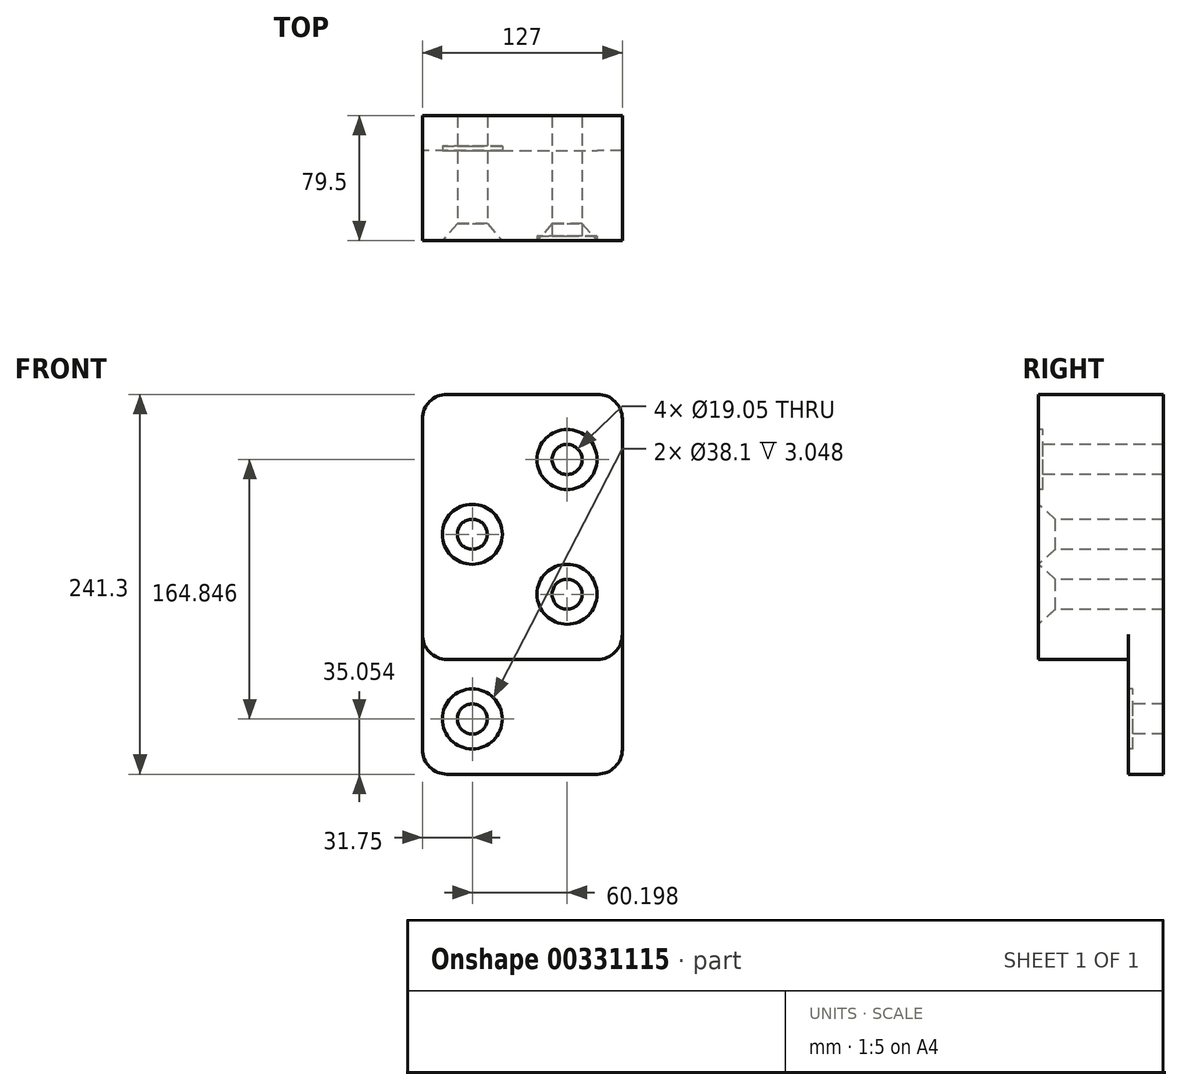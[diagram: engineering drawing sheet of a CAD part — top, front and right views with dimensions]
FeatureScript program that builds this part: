
annotation { "Feature Type Name" : "Feature", "Feature Type Description" : "" }
export const myFeature = defineFeature(function(context is Context, id is Id, definition is map)
    precondition{}
    {
        {
            var Q0;
            Q0=qCreatedBy(makeId("Front.planeOp"),FACE);
            var sketch = newSketch(context, id + "F0", { "sketchPlane" : qUnion([Q0])});
            skLineSegment(sketch, "E0.bottom", {"start": v(0, 0) * mm, "end": v(127, 0) * mm});
            skLineSegment(sketch, "E0.top", {"start": v(0, 168.4) * mm, "end": v(127, 168.4) * mm});
            skLineSegment(sketch, "E0.left", {"start": v(0, 0) * mm, "end": v(0, 168.4) * mm});
            skLineSegment(sketch, "E0.right", {"start": v(127, 0) * mm, "end": v(127, 168.4) * mm});
            skCircle(sketch, "E1", {"center": v(91.95, 41.4) * mm, "radius": 9.53 * mm});
            skCircle(sketch, "E2", {"center": v(91.95, 127) * mm, "radius": 9.53 * mm});
            skCircle(sketch, "E3", {"center": v(31.75, 79.5) * mm, "radius": 9.53 * mm});
            skSolve(sketch);
        }
        {
            var Q0;
            Q0=makeQuery(id+"F0.imprint","IMPRINT",FACE,{"disambiguationData":[TD([[makeQuery(id+"F0.imprint","IMPRINT",EDGE,{"derivedFrom":sQuery(id+"F0.wireOp",EDGE,"E0.top")}),-1.0]])]});
            var Q1;
            Q1=makeQuery(id+"F0.imprint","IMPRINT",FACE,{"disambiguationData":[TD([[makeQuery(id+"F0.imprint","IMPRINT",EDGE,{"derivedFrom":sQuery(id+"F0.wireOp",EDGE,"E2")}),1.0]])]});
            var Q2;
            Q2=makeQuery(id+"F0.imprint","IMPRINT",FACE,{"disambiguationData":[TD([[makeQuery(id+"F0.imprint","IMPRINT",EDGE,{"derivedFrom":sQuery(id+"F0.wireOp",EDGE,"E3")}),1.0]])]});
            var Q3;
            Q3=makeQuery(id+"F0.imprint","IMPRINT",FACE,{"disambiguationData":[TD([[makeQuery(id+"F0.imprint","IMPRINT",EDGE,{"derivedFrom":sQuery(id+"F0.wireOp",EDGE,"E1")}),1.0]])]});
            extrude(context, id + "F1", {"entities" : qUnion([Q0, Q1, Q2, Q3]), "oppositeDirection" : true, "depth" : 79.5 * mm});
        }
        {
            var Q0;
            Q0=sQuery(id+"F0.wireOp",VERTEX,"E3.center");
            var Q1;
            Q1=sQuery(id+"F0.wireOp",VERTEX,"E1.center");
            var Q2;
            Q2=makeQuery(id+"F1.opExtrude","SWEPT_BODY",BODY,{"disambiguationData":[OSD([sQuery(id+"F0.wireOp",EDGE,"E0.top"),sQuery(id+"F0.wireOp",EDGE,"E0.left"),sQuery(id+"F0.wireOp",EDGE,"E0.right"),sQuery(id+"F0.wireOp",EDGE,"PMlJOAfA-4wVx-9Cpc-nXHO-quy2oaBIfGFF.bottom")])]});
            hole(context, id + "F2", {"style" : HoleStyle.C_SINK, "endStyle" : HoleEndStyle.THROUGH, "holeDiameter" : 19.05 * mm, "cSinkDiameter" : 38.1 * mm, "cSinkAngle" : 82 * degree, "tappedDepth" : 12.7 * mm, "tapClearance" : 3, "locations" : qUnion([Q0, Q1]), "scope" : qUnion([Q2])});
        }
        {
            var Q0;
            Q0=makeQuery(id+"F1.opExtrude","CAP_FACE",FACE,{"disambiguationData":[OSD([sQuery(id+"F0.wireOp",EDGE,"E0.top"),sQuery(id+"F0.wireOp",EDGE,"E0.left"),sQuery(id+"F0.wireOp",EDGE,"E0.right"),sQuery(id+"F0.wireOp",EDGE,"PMlJOAfA-4wVx-9Cpc-nXHO-quy2oaBIfGFF.bottom")])],"isStart":false});
            var sketch = newSketch(context, id + "F3", { "sketchPlane" : qUnion([Q0])});
            skLineSegment(sketch, "E4.bottom", {"start": v(0, 0) * mm, "end": v(-127, 0) * mm});
            skLineSegment(sketch, "E4.top", {"start": v(0, -72.9) * mm, "end": v(-127, -72.9) * mm});
            skLineSegment(sketch, "E4.left", {"start": v(0, 0) * mm, "end": v(0, -72.9) * mm});
            skLineSegment(sketch, "E4.right", {"start": v(-127, 0) * mm, "end": v(-127, -72.9) * mm});
            skCircle(sketch, "E5", {"center": v(-31.75, -37.85) * mm, "radius": 9.53 * mm});
            skSolve(sketch);
        }
        {
            var Q0;
            Q0 = qSketchRegion(id + "F3", true);
            var Q1;
            Q1=makeQuery(id+"F3.imprint","IMPRINT",FACE,{"disambiguationData":[TD([[makeQuery(id+"F3.imprint","IMPRINT",EDGE,{"derivedFrom":sQuery(id+"F3.wireOp",EDGE,"E5")}),1.0]])]});
            extrude(context, id + "F4", {"entities" : qUnion([Q0, Q1]), "operationType" : NewBodyOperationType.ADD, "oppositeDirection" : true, "depth" : 22.35 * mm});
        }
        {
            var Q0;
            Q0=makeQuery(id+"F4.opExtrude","CAP_FACE",FACE,{"disambiguationData":[OSD([sQuery(id+"F3.wireOp",EDGE,"E4.bottom"),sQuery(id+"F3.wireOp",EDGE,"E4.top"),sQuery(id+"F3.wireOp",EDGE,"E4.left"),sQuery(id+"F3.wireOp",EDGE,"E4.right")])],"isStart":false});
            var sketch = newSketch(context, id + "F5", { "sketchPlane" : qUnion([Q0])});
            skLineSegment(sketch, "E6.bottom", {"start": v(127, -72.9) * mm, "end": v(0, -72.9) * mm});
            skLineSegment(sketch, "E6.top", {"start": v(127, 0) * mm, "end": v(0, 0) * mm});
            skLineSegment(sketch, "E6.left", {"start": v(127, -72.9) * mm, "end": v(127, 0) * mm});
            skLineSegment(sketch, "E6.right", {"start": v(0, -72.9) * mm, "end": v(0, 0) * mm});
            skCircle(sketch, "E7", {"center": v(31.75, -37.85) * mm, "radius": 9.53 * mm});
            skSolve(sketch);
        }
        {
            var Q0;
            Q0=sQuery(id+"F5.wireOp",VERTEX,"E7.center");
            var Q1;
            Q1=sQuery(id+"F0.wireOp",VERTEX,"E2.center");
            var Q2;
            Q2=makeQuery(id+"F1.opExtrude","SWEPT_BODY",BODY,{"disambiguationData":[OSD([sQuery(id+"F0.wireOp",EDGE,"E0.bottom"),sQuery(id+"F0.wireOp",EDGE,"E0.top"),sQuery(id+"F0.wireOp",EDGE,"E0.left"),sQuery(id+"F0.wireOp",EDGE,"E0.right")])]});
            hole(context, id + "F6", {"style" : HoleStyle.C_BORE, "endStyle" : HoleEndStyle.THROUGH, "holeDiameter" : 19.05 * mm, "cBoreDiameter" : 38.1 * mm, "cBoreDepth" : 3.05 * mm, "tappedDepth" : 12.7 * mm, "tapClearance" : 3, "locations" : qUnion([Q0, Q1]), "scope" : qUnion([Q2])});
        }
        {
            var Q0;
            Q0=makeQuery(id+"F1.opExtrude","SWEPT_EDGE",EDGE,{"disambiguationData":[OSD([sQuery(id+"F0.wireOp",EDGE,"E0.bottom"),sQuery(id+"F0.wireOp",EDGE,"E0.right")])]});
            fillet(context, id + "F7", {"entities" : qUnion([Q0]), "radius" : 15.75 * mm, "tangentPropagation" : true, "allowEdgeOverflow" : false});
        }
        {
            var Q0;
            Q0=makeQuery(id+"F1.opExtrude","SWEPT_EDGE",EDGE,{"disambiguationData":[OSD([sQuery(id+"F0.wireOp",EDGE,"E0.bottom"),sQuery(id+"F0.wireOp",EDGE,"E0.left")])]});
            var Q1;
            Q1=makeQuery(id+"F1.opExtrude","SWEPT_EDGE",EDGE,{"disambiguationData":[OSD([sQuery(id+"F0.wireOp",EDGE,"E0.top"),sQuery(id+"F0.wireOp",EDGE,"E0.left")])]});
            var Q2;
            Q2=makeQuery(id+"F1.opExtrude","SWEPT_EDGE",EDGE,{"disambiguationData":[OSD([sQuery(id+"F0.wireOp",EDGE,"E0.top"),sQuery(id+"F0.wireOp",EDGE,"E0.right")])]});
            fillet(context, id + "F8", {"entities" : qUnion([Q0, Q1, Q2]), "radius" : 15.75 * mm, "tangentPropagation" : true, "allowEdgeOverflow" : false});
        }
        {
            var Q0;
            Q0=makeQuery(id+"F4.opExtrude","SWEPT_EDGE",EDGE,{"disambiguationData":[OSD([sQuery(id+"F3.wireOp",EDGE,"E4.top"),sQuery(id+"F3.wireOp",EDGE,"E4.left")])]});
            var Q1;
            Q1=makeQuery(id+"F4.opExtrude","SWEPT_EDGE",EDGE,{"disambiguationData":[OSD([sQuery(id+"F3.wireOp",EDGE,"E4.top"),sQuery(id+"F3.wireOp",EDGE,"E4.right")])]});
            fillet(context, id + "F9", {"entities" : qUnion([Q0, Q1]), "radius" : 15.75 * mm, "tangentPropagation" : true, "allowEdgeOverflow" : false});
        }
    });
